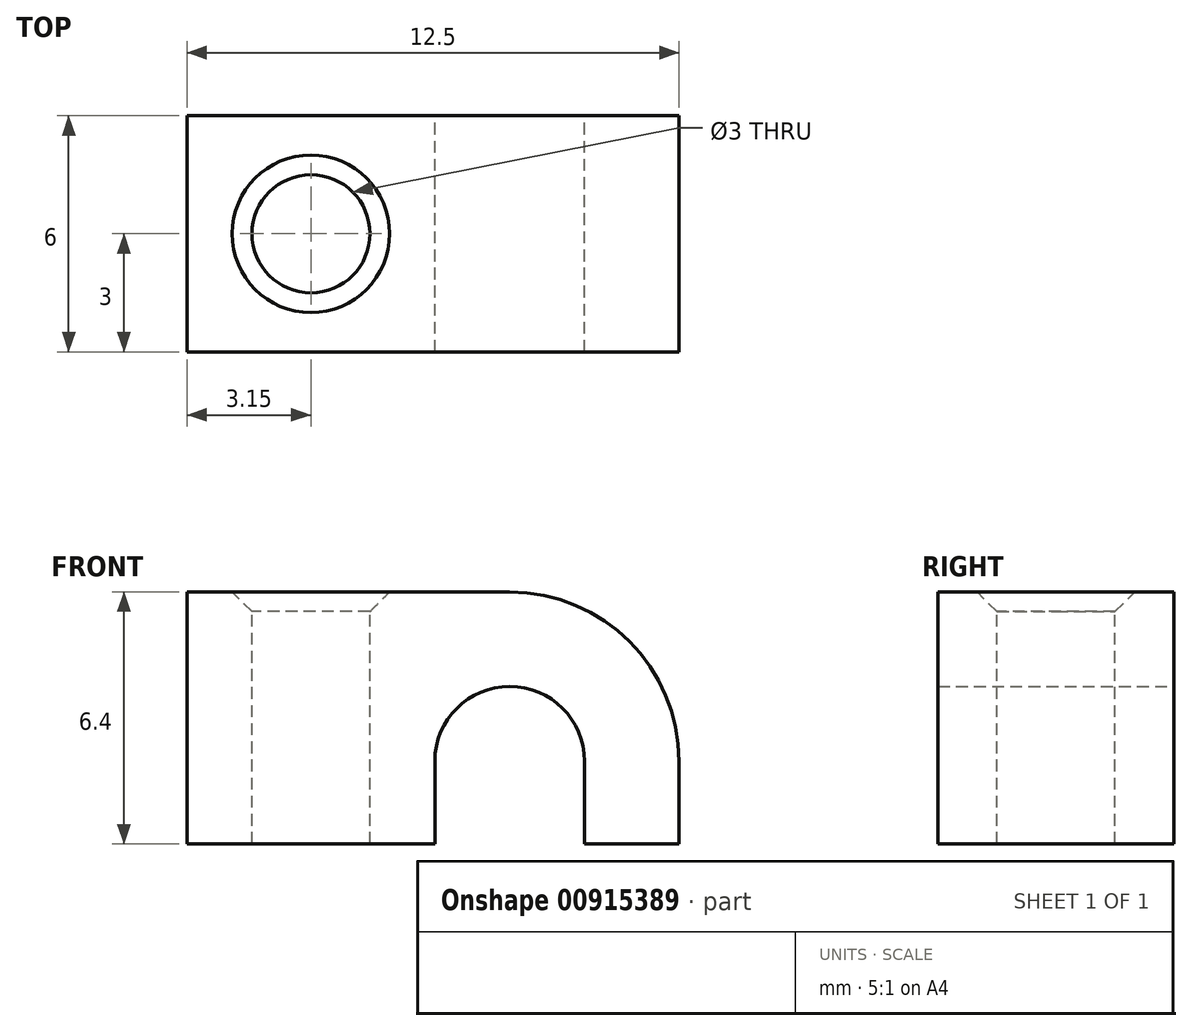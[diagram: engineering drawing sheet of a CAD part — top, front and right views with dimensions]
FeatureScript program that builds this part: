
annotation { "Feature Type Name" : "Feature", "Feature Type Description" : "" }
export const myFeature = defineFeature(function(context is Context, id is Id, definition is map)
    precondition{}
    {
        {
            var Q0;
            Q0=qCreatedBy(makeId("Front.planeOp"),FACE);
            var sketch = newSketch(context, id + "F0", { "sketchPlane" : qUnion([Q0])});
            skArc(sketch, "E0", {"start": v(12.5, 0) * mm, "mid": v(11.24, 3.04) * mm, "end": v(8.2, 4.3) * mm});
            skLineSegment(sketch, "E1", {"start": v(0, -2.1) * mm, "end": v(0, 4.3) * mm});
            skLineSegment(sketch, "E2", {"start": v(0, 4.3) * mm, "end": v(8.2, 4.3) * mm});
            skArc(sketch, "E3", {"start": v(10.1, 0) * mm, "mid": v(8.2, 1.9) * mm, "end": v(6.3, 0) * mm});
            skLineSegment(sketch, "E4", {"start": v(6.3, 0) * mm, "end": v(6.3, -2.1) * mm});
            skLineSegment(sketch, "E5", {"start": v(10.1, 0) * mm, "end": v(10.1, -2.1) * mm});
            skLineSegment(sketch, "E6", {"start": v(10.1, -2.1) * mm, "end": v(12.5, -2.1) * mm});
            skLineSegment(sketch, "E7", {"start": v(12.5, -2.1) * mm, "end": v(12.5, 0) * mm});
            skLineSegment(sketch, "E8", {"start": v(6.3, -2.1) * mm, "end": v(0, -2.1) * mm});
            skSolve(sketch);
        }
        {
            var Q0;
            {var subQ0=sQuery(id+"F0.wireOp",EDGE,"cL2L1XXM-q62j-7uNW-pd0z-jQs2hoirbVZH");Q0=makeQuery(id+"F0.imprint","IMPRINT",FACE,{"disambiguationData":[TD([[makeQuery(id+"F0.imprint","IMPRINT",EDGE,{"derivedFrom":subQ0}),1.0]])]});}
            var Q1;
            Q1=makeQuery(id+"F0.imprint","IMPRINT",FACE,{"disambiguationData":[TD([[makeQuery(id+"F0.imprint","IMPRINT",EDGE,{"derivedFrom":sQuery(id+"F0.wireOp",EDGE,"E3")}),-1.0]])]});
            extrude(context, id + "F1", {"entities" : qUnion([Q0, Q1]), "depth" : 6 * mm, "offsetDistance" : 25 * mm});
        }
        {
            var Q0;
            Q0=makeQuery(id+"F1.opExtrude","SWEPT_FACE",FACE,{"disambiguationData":[OSD([sQuery(id+"F0.wireOp",EDGE,"E2")])]});
            var sketch = newSketch(context, id + "F2", { "sketchPlane" : qUnion([Q0])});
            skLineSegment(sketch, "E9.0", {"start": v(6.3, -6) * mm, "end": v(6.3, 0) * mm, "construction": true});
            skLineSegment(sketch, "E10", {"start": v(6.3, -6) * mm, "end": v(0, 0) * mm, "construction": true});
            skPoint(sketch, "E11", {"position": v(3.15, -3) * mm});
            skSolve(sketch);
        }
        {
            var Q0;
            Q0=sQuery(id+"F2.wireOp",VERTEX,"E11");
            var Q1;
            Q1=makeQuery(id+"F1.opExtrude","SWEPT_BODY",BODY,{"disambiguationData":[OSD([sQuery(id+"F0.wireOp",EDGE,"cL2L1XXM-q62j-7uNW-pd0z-jQs2hoirbVZH"),sQuery(id+"F0.wireOp",EDGE,"E0"),sQuery(id+"F0.wireOp",EDGE,"E1"),sQuery(id+"F0.wireOp",EDGE,"E2"),sQuery(id+"F0.wireOp",EDGE,"E3"),sQuery(id+"F0.wireOp",EDGE,"CSNGDR7A-AkMN-3HGk-lJcl-lfmU78za7McH"),sQuery(id+"F0.wireOp",EDGE,"MJpTg79P-fTun-mrgq-yOEJ-SMPOCXVQTWgt")])]});
            hole(context, id + "F3", {"style" : HoleStyle.C_SINK, "endStyle" : HoleEndStyle.THROUGH, "holeDiameter" : 3 * mm, "cSinkDiameter" : 4 * mm, "cSinkAngle" : 90 * degree, "majorDiameter" : 5 * mm, "isTappedThrough" : true, "tappedDepth" : 12 * mm, "tapClearance" : 3, "locations" : qUnion([Q0]), "scope" : qUnion([Q1])});
        }
    });
